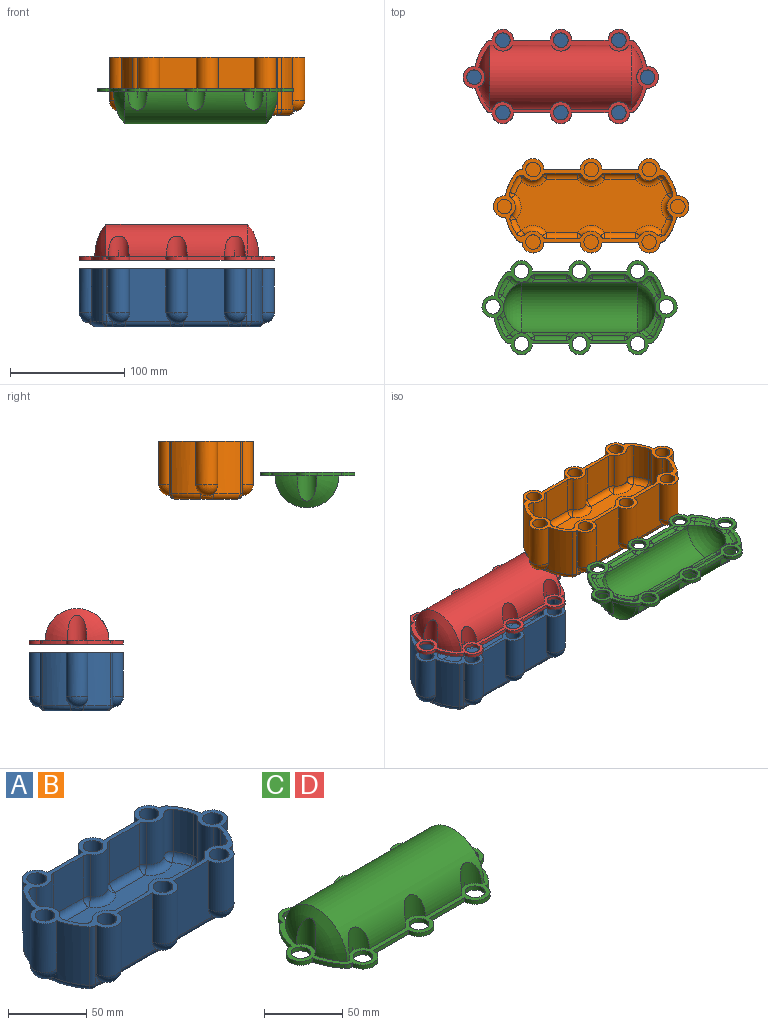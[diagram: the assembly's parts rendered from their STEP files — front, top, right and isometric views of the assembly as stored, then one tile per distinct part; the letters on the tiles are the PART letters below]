
ASSEMBLY  parts=4 mates=1
PART A: 144 faces, bbox 170.9x82.7x51 mm
  f0: cylinder r=46.85mm len=45.72mm, axis (0,0,-1), area 1031.7mm2, adj f1,f57,f58,f59,f60
  f1: cylinder r=9.53mm len=38.1mm, axis (0,0,-1), area 1214mm2, adj f0,f2,f54,f57,f60
  f2: cylinder r=46.85mm len=45.72mm, axis (0,0,-1), area 1091.9mm2, adj f1,f3,f53,f57,f60
  f3: cylinder r=5.08mm len=45.72mm, axis (0,0,-1), area 204mm2, adj f2,f4,f52,f60
  f4: plane 45.72x4.68mm, normal (0,1,0), area 48.6mm2, adj f3,f5,f50,f51,f60
  f5: cylinder r=9.53mm len=38.1mm, axis (0,0,-1), area 1140.1mm2, adj f4,f6,f50,f60
  f6: plane 45.72x39.37mm, normal (0,1,0), area 1469.1mm2, adj f5,f7,f48,f49,f50,f60
  f7: cylinder r=9.53mm len=38.1mm, axis (0,0,-1), area 1140.1mm2, adj f6,f8,f48,f60
  f8: plane 45.72x39.37mm, normal (0,1,0), area 1469.1mm2, adj f7,f9,f46,f47,f48,f60
  f9: cylinder r=9.53mm len=38.1mm, axis (0,0,-1), area 1140.1mm2, adj f8,f10,f46,f60
  f10: plane 45.72x4.68mm, normal (0,1,0), area 48.6mm2, adj f9,f11,f45,f46,f60
  f11: cylinder r=5.08mm len=45.72mm, axis (0,0,-1), area 204mm2, adj f10,f12,f44,f60
  f12: cylinder r=46.85mm len=45.72mm, axis (0,0,-1), area 1091.9mm2, adj f11,f13,f42,f43,f60
  f13: cylinder r=9.53mm len=38.1mm, axis (0,0,-1), area 1214mm2, adj f12,f14,f42,f60
  f14: cylinder r=46.85mm len=45.72mm, axis (0,0,-1), area 1031.7mm2, adj f13,f15,f41,f42,f60
  f15: cylinder r=5.08mm len=45.72mm, axis (0,0,-1), area 204mm2, adj f14,f16,f40,f60
  f16: plane 45.72x4.68mm, normal (0,-1,0), area 48.6mm2, adj f15,f17,f38,f39,f60
  f17: cylinder r=9.53mm len=38.1mm, axis (0,0,-1), area 1140.1mm2, adj f16,f18,f38,f60
  f18: plane 45.72x39.37mm, normal (0,-1,0), area 1469.1mm2, adj f17,f19,f36,f37,f38,f60
  f19: cylinder r=9.53mm len=38.1mm, axis (0,0,-1), area 1140.1mm2, adj f18,f20,f36,f60
  f20: plane 45.72x39.37mm, normal (0,-1,0), area 1469.1mm2, adj f19,f21,f34,f35,f36,f60
  f21: cylinder r=9.53mm len=38.1mm, axis (0,0,-1), area 1140.1mm2, adj f20,f22,f34,f60
  f22: plane 45.72x4.68mm, normal (0,-1,0), area 48.6mm2, adj f21,f23,f34,f59,f60
  f23: cylinder r=5.08mm len=5.08mm, axis (1,0,0), area 37.4mm2, adj f22,f24,f25,f26
  f24: bspline ~11.43x5.08mm, area 76.3mm2, adj f23,f26,f34,f35
  f25: sphere r=5.08mm, area 22.7mm2, adj f23,f58,f59
  f26: plane 142.38x54.09mm, normal (0,0,-1), area 7247.3mm2, adj f23,f24,f27,f28,f29,f30,f31,f32
  f27: bspline ~13.47x6.35mm, area 73.1mm2, adj f26,f53,f57,f58
  f28: bspline ~11.43x5.08mm, area 76.3mm2, adj f26,f49,f50,f51
  f29: bspline ~11.43x5.08mm, area 76.3mm2, adj f26,f47,f48,f49
  f30: bspline ~11.43x5.08mm, area 76.3mm2, adj f26,f45,f46,f47
  f31: bspline ~12.51x5.74mm, area 73.1mm2, adj f26,f41,f42,f43
  f32: bspline ~11.43x5.08mm, area 76.3mm2, adj f26,f37,f38,f39
  f33: bspline ~11.43x5.08mm, area 76.3mm2, adj f26,f35,f36,f37
  f34: sphere r=9.53mm, area 285mm2, adj f20,f21,f22,f24
  f35: cylinder r=5.08mm len=39.37mm, axis (1,0,0), area 314.2mm2, adj f20,f24,f26,f33
  f36: sphere r=9.53mm, area 285mm2, adj f18,f19,f20,f33
  f37: cylinder r=5.08mm len=39.37mm, axis (1,0,0), area 314.2mm2, adj f18,f26,f32,f33
  f38: sphere r=9.53mm, area 285mm2, adj f16,f17,f18,f32
  f39: cylinder r=5.08mm len=5.08mm, axis (1,0,0), area 37.4mm2, adj f16,f26,f32,f40
  f40: sphere r=5.08mm, area 22.7mm2, adj f15,f39,f41
  f41: torus R=41.77mm, axis (0,0,-1), area 199.8mm2, adj f14,f26,f31,f40
  f42: sphere r=9.53mm, area 299.5mm2, adj f12,f13,f14,f31
  f43: torus R=41.77mm, axis (0,0,-1), area 209.9mm2, adj f12,f26,f31,f44
  f44: sphere r=5.08mm, area 22.7mm2, adj f11,f43,f45
  f45: cylinder r=5.08mm len=5.08mm, axis (1,0,0), area 37.4mm2, adj f10,f26,f30,f44
  f46: sphere r=9.53mm, area 285mm2, adj f8,f9,f10,f30
  f47: cylinder r=5.08mm len=39.37mm, axis (1,0,0), area 314.2mm2, adj f8,f26,f29,f30
  f48: sphere r=9.53mm, area 285mm2, adj f6,f7,f8,f29
  f49: cylinder r=5.08mm len=39.37mm, axis (1,0,0), area 314.2mm2, adj f6,f26,f28,f29
  f50: sphere r=9.53mm, area 285mm2, adj f4,f5,f6,f28
  f51: cylinder r=5.08mm len=5.08mm, axis (1,0,0), area 37.4mm2, adj f4,f26,f28,f52
  f52: sphere r=5.08mm, area 29.2mm2, adj f3,f51,f53
  f53: torus R=41.77mm, axis (0,0,-1), area 209.9mm2, adj f2,f26,f27,f52
  f54: plane 9.63x0.37mm, normal (0,0,-1), area 1.2mm2, adj f1,f55,f56
  f55: cylinder r=46.85mm len=2.63mm, axis (0,0,-1), area 0mm2, adj f54,f56
  f56: cone r=0mm half-angle=0.8deg, axis (0,1,0), area 2.3mm2, adj f54,f55,f57
  f57: sphere r=9.53mm, area 299.5mm2, adj f0,f1,f2,f27,f56
  f58: torus R=41.77mm, axis (0,0,-1), area 199.8mm2, adj f0,f25,f26,f27
  f59: cylinder r=5.08mm len=45.72mm, axis (0,0,-1), area 204mm2, adj f0,f22,f25,f60
  f60: plane 170.84x82.55mm, normal (0,0,1), area 2063.6mm2, adj f0,f1,f2,f3,f4,f5,f6,f7
  f61: cylinder r=6.35mm len=25.4mm, axis (0,0,-1), area 1013.4mm2, adj f60,f62
  f62: plane 12.7x12.7mm, normal (0,0,1), area 126.7mm2, adj f61
  f63: cylinder r=6.35mm len=25.4mm, axis (0,0,-1), area 1013.4mm2, adj f60,f64
  f64: plane 12.7x12.7mm, normal (0,0,1), area 126.7mm2, adj f63
  f65: cylinder r=6.35mm len=25.4mm, axis (0,0,-1), area 1013.4mm2, adj f60,f66
  f66: plane 12.7x12.7mm, normal (0,0,1), area 126.7mm2, adj f65
  f67: cylinder r=6.35mm len=25.4mm, axis (0,0,-1), area 1013.4mm2, adj f60,f68
  f68: plane 12.7x12.7mm, normal (0,0,1), area 126.7mm2, adj f67
  f69: cylinder r=6.35mm len=25.4mm, axis (0,0,-1), area 1013.4mm2, adj f60,f70
  f70: plane 12.7x12.7mm, normal (0,0,1), area 126.7mm2, adj f69
  f71: cylinder r=6.35mm len=25.4mm, axis (0,0,-1), area 1013.4mm2, adj f60,f72
  f72: plane 12.7x12.7mm, normal (0,0,1), area 126.7mm2, adj f71
  f73: cylinder r=6.35mm len=25.4mm, axis (0,0,-1), area 1013.4mm2, adj f60,f74
  f74: plane 12.7x12.7mm, normal (0,0,1), area 126.7mm2, adj f73
  f75: cylinder r=6.35mm len=25.4mm, axis (0,0,-1), area 1013.4mm2, adj f60,f76
  f76: plane 12.7x12.7mm, normal (0,0,1), area 126.7mm2, adj f75
  f77: cylinder r=5.08mm len=33.02mm, axis (0,0,-1), area 162.7mm2, adj f60,f78,f113,f143
  f78: sphere r=5.08mm, area 25mm2, adj f77,f79,f112
  f79: cylinder r=5.08mm len=26.7mm, axis (1,0,0), area 213.1mm2, adj f78,f80,f111,f143
  f80: plane 132.49x46.99mm, normal (0,0,1), area 5298.6mm2, adj f79,f81,f83,f85,f87,f90,f92,f94
  f81: torus R=14.61mm, axis (0,0,-1), area 159.4mm2, adj f80,f82,f111,f141
  f82: sphere r=5.08mm, area 45.6mm2, adj f81,f83,f140
  f83: torus R=38.59mm, axis (0,0,-1), area 97mm2, adj f80,f82,f84,f139
  f84: sphere r=5.08mm, area 28.9mm2, adj f83,f85,f138
  f85: torus R=14.61mm, axis (0,0,-1), area 151.5mm2, adj f80,f84,f86,f137
  f86: sphere r=5.08mm, area 28.9mm2, adj f85,f87,f136
  f87: torus R=38.59mm, axis (0,0,-1), area 123.2mm2, adj f80,f86,f88,f90,f134,f135
  f88: sphere r=5.08mm, area 3.1mm2, adj f87,f89,f90,f134
  f89: sphere r=5.08mm, area 0mm2, adj f88,f90,f134
  f90: torus R=14.61mm, axis (0,0,-1), area 171.7mm2, adj f80,f87,f88,f89,f91,f133,f134
  f91: sphere r=5.08mm, area 25mm2, adj f90,f92,f132
  f92: cylinder r=5.08mm len=26.7mm, axis (-1,0,0), area 213.1mm2, adj f80,f91,f93,f131
  f93: sphere r=5.08mm, area 30.7mm2, adj f92,f94,f130
  f94: torus R=14.61mm, axis (0,0,-1), area 176mm2, adj f80,f93,f95,f129
  f95: sphere r=5.08mm, area 25mm2, adj f94,f96,f128
  f96: cylinder r=5.08mm len=26.7mm, axis (-1,0,0), area 213.1mm2, adj f80,f95,f97,f127
  f97: sphere r=5.08mm, area 30.7mm2, adj f96,f98,f126
  f98: torus R=14.61mm, axis (0,0,-1), area 159.4mm2, adj f80,f97,f99,f125
  f99: sphere r=5.08mm, area 51.2mm2, adj f98,f100,f124
  f100: torus R=38.59mm, axis (0,0,-1), area 106.4mm2, adj f80,f99,f101,f123
  f101: sphere r=5.08mm, area 26.3mm2, adj f100,f102,f122
  f102: torus R=14.61mm, axis (0,0,-1), area 151.5mm2, adj f80,f101,f103,f121
  f103: sphere r=5.08mm, area 18.4mm2, adj f102,f104,f120
  f104: torus R=38.59mm, axis (0,0,-1), area 113.8mm2, adj f80,f103,f105,f107,f118,f119
  f105: sphere r=5.08mm, area 3.1mm2, adj f104,f106,f107,f118
  f106: sphere r=5.08mm, area 0mm2, adj f105,f107,f118
  f107: torus R=14.61mm, axis (0,0,-1), area 171.7mm2, adj f80,f104,f105,f106,f108,f117,f118
  f108: sphere r=5.08mm, area 25mm2, adj f107,f109,f116
  f109: cylinder r=5.08mm len=26.7mm, axis (1,0,0), area 213.1mm2, adj f80,f108,f110,f115
  f110: sphere r=5.08mm, area 25mm2, adj f109,f112,f114
  f111: sphere r=5.08mm, area 25mm2, adj f79,f81,f142
  f112: torus R=14.61mm, axis (0,0,-1), area 176mm2, adj f78,f80,f110,f113
  f113: cylinder r=9.53mm len=33.02mm, axis (0,0,-1), area 610.2mm2, adj f60,f77,f112,f114
  f114: cylinder r=5.08mm len=33.02mm, axis (0,0,-1), area 162.7mm2, adj f60,f110,f113,f115
  f115: plane 33.02x26.7mm, normal (0,1,0), area 881.7mm2, adj f60,f109,f114,f116
  f116: cylinder r=5.08mm len=33.02mm, axis (0,0,-1), area 162.7mm2, adj f60,f108,f115,f117
  f117: cylinder r=9.53mm len=33.02mm, axis (0,0,-1), area 552.6mm2, adj f60,f107,f116,f118
  f118: cylinder r=5.08mm len=36.9mm, axis (0,0,-1), area 316.2mm2, adj f60,f104,f105,f106,f107,f117,f119
  f119: cylinder r=43.67mm len=33.02mm, axis (0,0,-1), area 419.1mm2, adj f60,f104,f118,f120
  f120: cylinder r=5.08mm len=33.02mm, axis (0,0,-1), area 187.7mm2, adj f60,f103,f119,f121
  f121: cylinder r=9.53mm len=33.02mm, axis (0,0,-1), area 525.1mm2, adj f60,f102,f120,f122
  f122: cylinder r=5.08mm len=33.02mm, axis (0,0,-1), area 187.7mm2, adj f60,f101,f121,f123
  f123: cylinder r=43.67mm len=33.02mm, axis (0,0,-1), area 459.6mm2, adj f60,f100,f122,f124
  f124: cylinder r=5.08mm len=33.02mm, axis (0,0,-1), area 296.7mm2, adj f60,f99,f123,f125
  f125: cylinder r=9.53mm len=33.02mm, axis (0,0,-1), area 552.6mm2, adj f60,f98,f124,f126
  f126: cylinder r=5.08mm len=33.02mm, axis (0,0,-1), area 162.7mm2, adj f60,f97,f125,f127
  f127: plane 33.02x26.7mm, normal (0,-1,0), area 881.7mm2, adj f60,f96,f126,f128
  f128: cylinder r=5.08mm len=33.02mm, axis (0,0,-1), area 162.7mm2, adj f60,f95,f127,f129
  f129: cylinder r=9.53mm len=33.02mm, axis (0,0,-1), area 610.2mm2, adj f60,f94,f128,f130
  f130: cylinder r=5.08mm len=33.02mm, axis (0,0,-1), area 162.7mm2, adj f60,f93,f129,f131
  f131: plane 33.02x26.7mm, normal (0,-1,0), area 881.7mm2, adj f60,f92,f130,f132
  f132: cylinder r=5.08mm len=33.02mm, axis (0,0,-1), area 162.7mm2, adj f60,f91,f131,f133
  f133: cylinder r=9.53mm len=33.02mm, axis (0,0,-1), area 552.6mm2, adj f60,f90,f132,f134
  f134: cylinder r=5.08mm len=36.9mm, axis (0,0,-1), area 316.2mm2, adj f60,f87,f88,f89,f90,f133,f135
  f135: cylinder r=43.67mm len=33.02mm, axis (0,0,-1), area 459.6mm2, adj f60,f87,f134,f136
  f136: cylinder r=5.08mm len=33.02mm, axis (0,0,-1), area 187.7mm2, adj f60,f86,f135,f137
  f137: cylinder r=9.53mm len=33.02mm, axis (0,0,-1), area 525.1mm2, adj f60,f85,f136,f138
  f138: cylinder r=5.08mm len=33.02mm, axis (0,0,-1), area 187.7mm2, adj f60,f84,f137,f139
  f139: cylinder r=43.67mm len=33.02mm, axis (0,0,-1), area 419.1mm2, adj f60,f83,f138,f140
  f140: cylinder r=5.08mm len=33.02mm, axis (0,0,-1), area 296.7mm2, adj f60,f82,f139,f141
  f141: cylinder r=9.53mm len=33.02mm, axis (0,0,-1), area 552.6mm2, adj f60,f81,f140,f142
  f142: cylinder r=5.08mm len=33.02mm, axis (0,0,-1), area 162.7mm2, adj f60,f111,f141,f143
  f143: plane 33.02x26.7mm, normal (0,1,0), area 881.7mm2, adj f60,f77,f79,f142
PART B: same geometry as A
PART C: 88 faces, bbox 170.9x82.6x51.8 mm
  f0: cylinder r=27.92mm len=124.16mm, axis (-1,0,0), area 9332.4mm2, adj f4,f5,f38,f49,f50,f51,f53,f54
  f1: cylinder r=6.35mm len=12.7mm, axis (0,0,-1), area 126.7mm2, adj f38,f39
  f2: cylinder r=6.35mm len=12.7mm, axis (0,0,-1), area 126.7mm2, adj f38,f39
  f3: cylinder r=6.35mm len=12.7mm, axis (0,0,-1), area 126.7mm2, adj f38,f39
  f4: revolved ~55.83x27.92mm, area 1072.4mm2, adj f0,f38,f52
  f5: revolved ~55.83x27.92mm, area 1072.4mm2, adj f0,f38,f48
  f6: cylinder r=6.35mm len=12.7mm, axis (0,0,-1), area 126.7mm2, adj f38,f39
  f7: cylinder r=6.35mm len=12.7mm, axis (0,0,-1), area 126.7mm2, adj f38,f39
  f8: cylinder r=6.35mm len=12.7mm, axis (0,0,-1), area 126.7mm2, adj f38,f39
  f9: cylinder r=6.35mm len=12.7mm, axis (0,0,-1), area 126.7mm2, adj f38,f39
  f10: cylinder r=6.35mm len=12.7mm, axis (0,0,-1), area 126.7mm2, adj f38,f39
  f11: plane 16.5x11.85mm, normal (0,0,-1), area 70mm2, adj f43,f64,f65,f66
  f12: plane 32.48x2.66mm, normal (0,0,-1), area 80.3mm2, adj f42,f60,f61,f63
  f13: plane 32.48x2.66mm, normal (0,0,-1), area 80.3mm2, adj f42,f62,f63,f64
  f14: plane 16.5x11.85mm, normal (0,0,-1), area 70mm2, adj f41,f56,f60,f71
  f15: plane 32.48x2.66mm, normal (0,0,-1), area 80.3mm2, adj f42,f58,f59,f70
  f16: plane 32.48x2.66mm, normal (0,0,-1), area 80.3mm2, adj f42,f67,f68,f70
  f17: plane 15.61x11.55mm, normal (0,0,-1), area 66.6mm2, adj f41,f56,f57,f59
  f18: plane 3.18x0.87mm, normal (0,-1,0), area 2.8mm2, adj f19,f38,f39,f47
  f19: cylinder r=9.53mm len=19.05mm, axis (0,0,-1), area 95mm2, adj f18,f20,f38,f39
  f20: plane 31.75x3.18mm, normal (0,-1,0), area 100.8mm2, adj f19,f21,f38,f39
  f21: cylinder r=9.53mm len=19.05mm, axis (0,0,-1), area 95mm2, adj f20,f22,f38,f39
  f22: plane 31.75x3.18mm, normal (0,-1,0), area 100.8mm2, adj f21,f23,f38,f39
  f23: cylinder r=9.53mm len=19.05mm, axis (0,0,-1), area 95mm2, adj f22,f24,f38,f39
  f24: plane 3.18x0.87mm, normal (0,-1,0), area 2.8mm2, adj f23,f38,f39,f44
  f25: cylinder r=46.85mm len=19.79mm, axis (0,0,-1), area 70.6mm2, adj f26,f38,f39,f44
  f26: cylinder r=9.53mm len=19.05mm, axis (0,0,-1), area 101.2mm2, adj f25,f27,f38,f39
  f27: cylinder r=46.85mm len=21.08mm, axis (0,0,-1), area 74.8mm2, adj f26,f38,f39,f45
  f28: plane 3.18x0.87mm, normal (0,1,0), area 2.8mm2, adj f29,f38,f39,f45
  f29: cylinder r=9.53mm len=19.05mm, axis (0,0,-1), area 95mm2, adj f28,f30,f38,f39
  f30: plane 31.75x3.18mm, normal (0,1,0), area 100.8mm2, adj f29,f31,f38,f39
  f31: cylinder r=9.53mm len=19.05mm, axis (0,0,-1), area 95mm2, adj f30,f32,f38,f39
  f32: plane 31.75x3.18mm, normal (0,1,0), area 100.8mm2, adj f31,f33,f38,f39
  f33: cylinder r=9.53mm len=19.05mm, axis (0,0,-1), area 95mm2, adj f32,f34,f38,f39
  f34: plane 3.18x0.87mm, normal (0,1,0), area 2.8mm2, adj f33,f38,f39,f46
  f35: cylinder r=46.85mm len=21.08mm, axis (0,0,-1), area 74.8mm2, adj f36,f38,f39,f46
  f36: cylinder r=9.53mm len=19.05mm, axis (0,0,-1), area 101.2mm2, adj f35,f37,f38,f39
  f37: cylinder r=46.85mm len=19.79mm, axis (0,0,-1), area 70.6mm2, adj f36,f38,f39,f47
  f38: plane 170.84x82.55mm, normal (0,0,1), area 2128.1mm2, adj f0,f1,f2,f3,f4,f5,f6,f7
  f39: plane 170.88x82.59mm, normal (0,0,-1), area 2037.8mm2, adj f1,f2,f3,f6,f7,f8,f9,f10
  f40: plane 15.61x11.55mm, normal (0,0,-1), area 66.6mm2, adj f43,f65,f68,f69
  f41: sphere r=23.64mm, area 1176.7mm2, adj f14,f17,f42,f56,f59,f60
  f42: cylinder r=22.23mm len=101.6mm, axis (1,0,0), area 7149.6mm2, adj f12,f13,f15,f16,f41,f43,f59,f60
  f43: sphere r=23.64mm, area 1177.6mm2, adj f11,f40,f42,f64,f65,f68
  f44: cylinder r=5.08mm len=3.91mm, axis (0,0,-1), area 14.2mm2, adj f24,f25,f38,f39
  f45: cylinder r=5.08mm len=3.91mm, axis (0,0,-1), area 14.2mm2, adj f27,f28,f38,f39
  f46: cylinder r=5.08mm len=3.91mm, axis (0,0,-1), area 14.2mm2, adj f34,f35,f38,f39
  f47: cylinder r=5.08mm len=3.91mm, axis (0,0,-1), area 14.2mm2, adj f18,f37,f38,f39
  f48: cylinder r=9.53mm len=22.03mm, axis (0,0,-1), area 362.9mm2, adj f5,f38
  f49: cylinder r=9.53mm len=17.96mm, axis (0,0,-1), area 326.3mm2, adj f0,f38
  f50: cylinder r=9.53mm len=17.96mm, axis (0,0,-1), area 326.3mm2, adj f0,f38
  f51: cylinder r=9.53mm len=17.96mm, axis (0,0,-1), area 326.3mm2, adj f0,f38
  f52: cylinder r=9.53mm len=22.03mm, axis (0,0,-1), area 362.9mm2, adj f4,f38
  f53: cylinder r=9.53mm len=16.8mm, axis (0,0,-1), area 258.3mm2, adj f0,f38
  f54: cylinder r=9.53mm len=16.8mm, axis (0,0,-1), area 258.3mm2, adj f0,f38
  f55: cylinder r=9.53mm len=16.8mm, axis (0,0,-1), area 258.3mm2, adj f0,f38
  f56: torus R=13.21mm, axis (0,0,1), area 43.2mm2, adj f14,f17,f39,f41,f84,f87
  f57: torus R=39.98mm, axis (0,0,-1), area 62mm2, adj f17,f39,f84,f85
  f58: cylinder r=5.08mm len=28.22mm, axis (-1,0,0), area 116.5mm2, adj f15,f39,f74,f86
  f59: torus R=13.21mm, axis (0,0,1), area 55.8mm2, adj f15,f17,f39,f41,f42,f85,f86
  f60: torus R=13.21mm, axis (0,0,1), area 55.8mm2, adj f12,f14,f39,f41,f42,f72,f81
  f61: cylinder r=5.08mm len=28.22mm, axis (-1,0,0), area 116.5mm2, adj f12,f39,f81,f82
  f62: cylinder r=5.08mm len=28.22mm, axis (1,0,0), area 116.5mm2, adj f13,f39,f78,f83
  f63: torus R=13.21mm, axis (0,0,1), area 45.9mm2, adj f12,f13,f39,f42,f82,f83
  f64: torus R=13.21mm, axis (0,0,1), area 55.8mm2, adj f11,f13,f39,f42,f43,f78,f79
  f65: torus R=13.21mm, axis (0,0,1), area 43.2mm2, adj f11,f39,f40,f43,f75,f80
  f66: torus R=39.98mm, axis (0,0,-1), area 66.9mm2, adj f11,f39,f79,f80
  f67: cylinder r=5.08mm len=28.22mm, axis (1,0,0), area 116.5mm2, adj f16,f39,f73,f76
  f68: torus R=13.21mm, axis (0,0,1), area 55.8mm2, adj f16,f39,f40,f42,f43,f76,f77
  f69: torus R=39.98mm, axis (0,0,-1), area 62mm2, adj f39,f40,f75,f77
  f70: torus R=13.21mm, axis (0,0,1), area 45.9mm2, adj f15,f16,f39,f42,f73,f74
  f71: torus R=39.98mm, axis (0,0,-1), area 66.9mm2, adj f14,f39,f72,f87
  f72: sphere r=5.08mm, area 15mm2, adj f39,f60,f71
  f73: sphere r=5.08mm, area 8.3mm2, adj f39,f67,f70
  f74: sphere r=5.08mm, area 8.3mm2, adj f39,f58,f70
  f75: sphere r=5.08mm, area 9.4mm2, adj f39,f65,f69
  f76: sphere r=5.08mm, area 8.3mm2, adj f39,f67,f68
  f77: sphere r=5.08mm, area 14.9mm2, adj f39,f68,f69
  f78: sphere r=5.08mm, area 8.3mm2, adj f39,f62,f64
  f79: sphere r=5.08mm, area 16.7mm2, adj f39,f64,f66
  f80: sphere r=5.08mm, area 9.4mm2, adj f39,f65,f66
  f81: sphere r=5.08mm, area 9.8mm2, adj f39,f60,f61
  f82: sphere r=5.08mm, area 8.3mm2, adj f39,f61,f63
  f83: sphere r=5.08mm, area 9.8mm2, adj f39,f62,f63
  f84: sphere r=5.08mm, area 9.4mm2, adj f39,f56,f57
  f85: sphere r=5.08mm, area 14.9mm2, adj f39,f57,f59
  f86: sphere r=5.08mm, area 8.3mm2, adj f39,f58,f59
  f87: sphere r=5.08mm, area 9.4mm2, adj f39,f56,f71
PART D: same geometry as C
PLACE A t=(-68.77,-108.64,-27.54)mm
PLACE B t=(-42.27,-222.12,157.63)mm
PLACE C rot(axis=(1,0,0),180deg) t=(-52.38,-309.77,155.78)mm
PLACE D t=(-68.77,-108.64,5.54)mm
MATE slider D.f10 <-> A.f75  axis (0,0,-1) through (7.13,-108.64,5.54)mm
